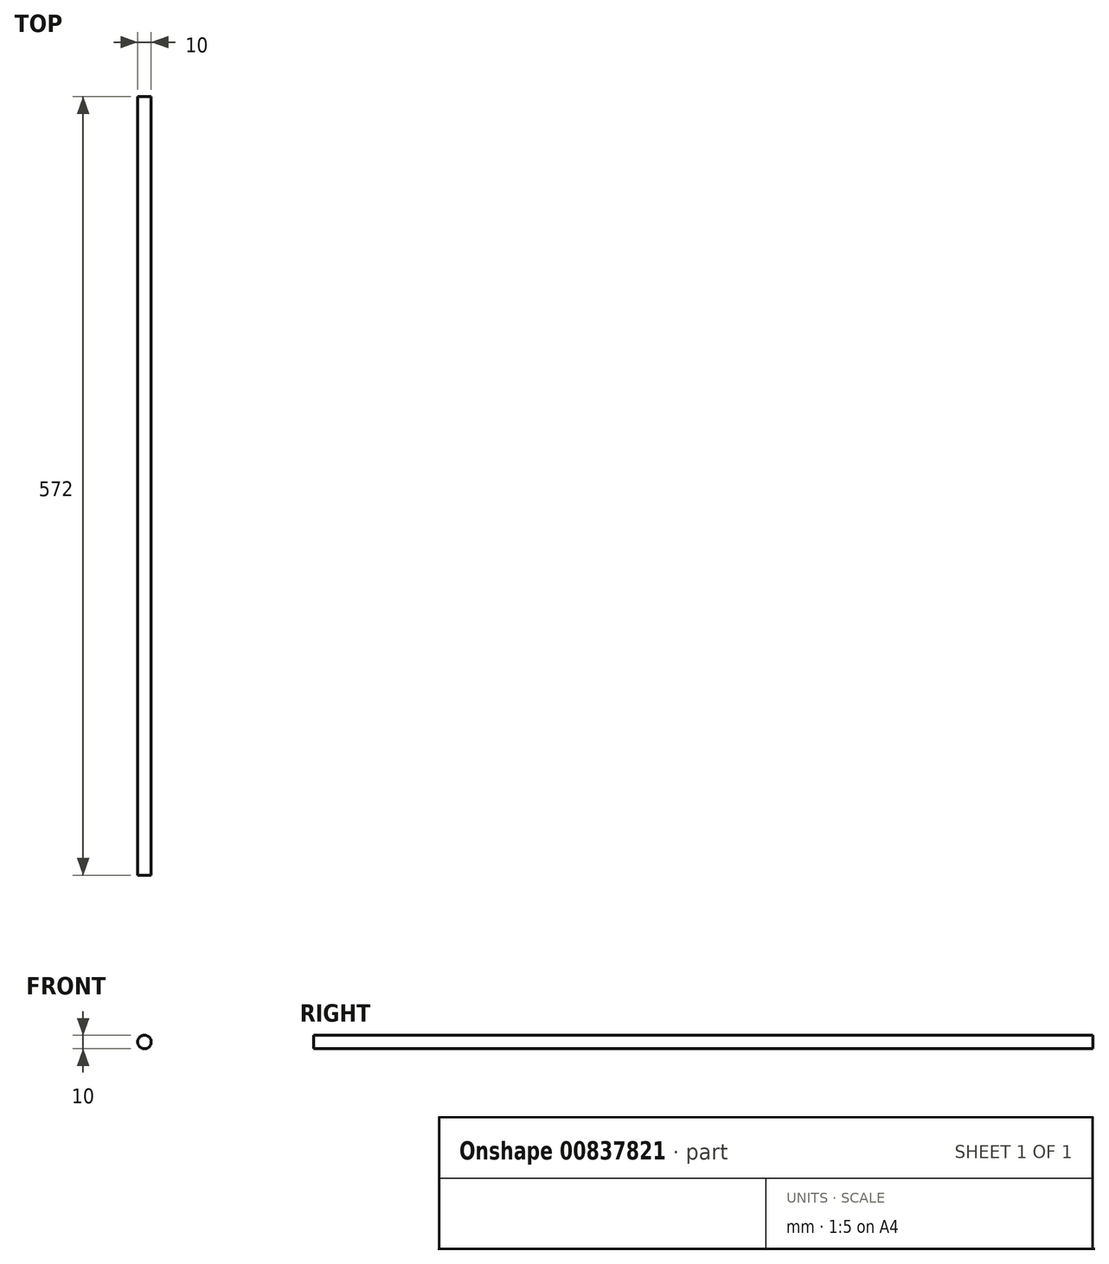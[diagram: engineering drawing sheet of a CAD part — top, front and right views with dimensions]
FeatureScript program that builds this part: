
annotation { "Feature Type Name" : "Feature", "Feature Type Description" : "" }
export const myFeature = defineFeature(function(context is Context, id is Id, definition is map)
    precondition{}
    {
        {
            var Q0;
            Q0=qCreatedBy(makeId("Front.planeOp"),FACE);
            var sketch = newSketch(context, id + "F0", { "sketchPlane" : qUnion([Q0])});
            skCircle(sketch, "E0", {"center": v(0, 0) * mm, "radius": 5 * mm});
            skSolve(sketch);
        }
        {
            var Q0;
            Q0=makeQuery(id+"F0.imprint","IMPRINT",FACE,{"disambiguationData":[TD([[makeQuery(id+"F0.imprint","IMPRINT",EDGE,{"derivedFrom":sQuery(id+"F0.wireOp",EDGE,"E0")}),1.0]])]});
            extrude(context, id + "F1", {"entities" : qUnion([Q0]), "depth" : (582 - 10) * mm, "offsetDistance" : 25 * mm});
        }
    });
